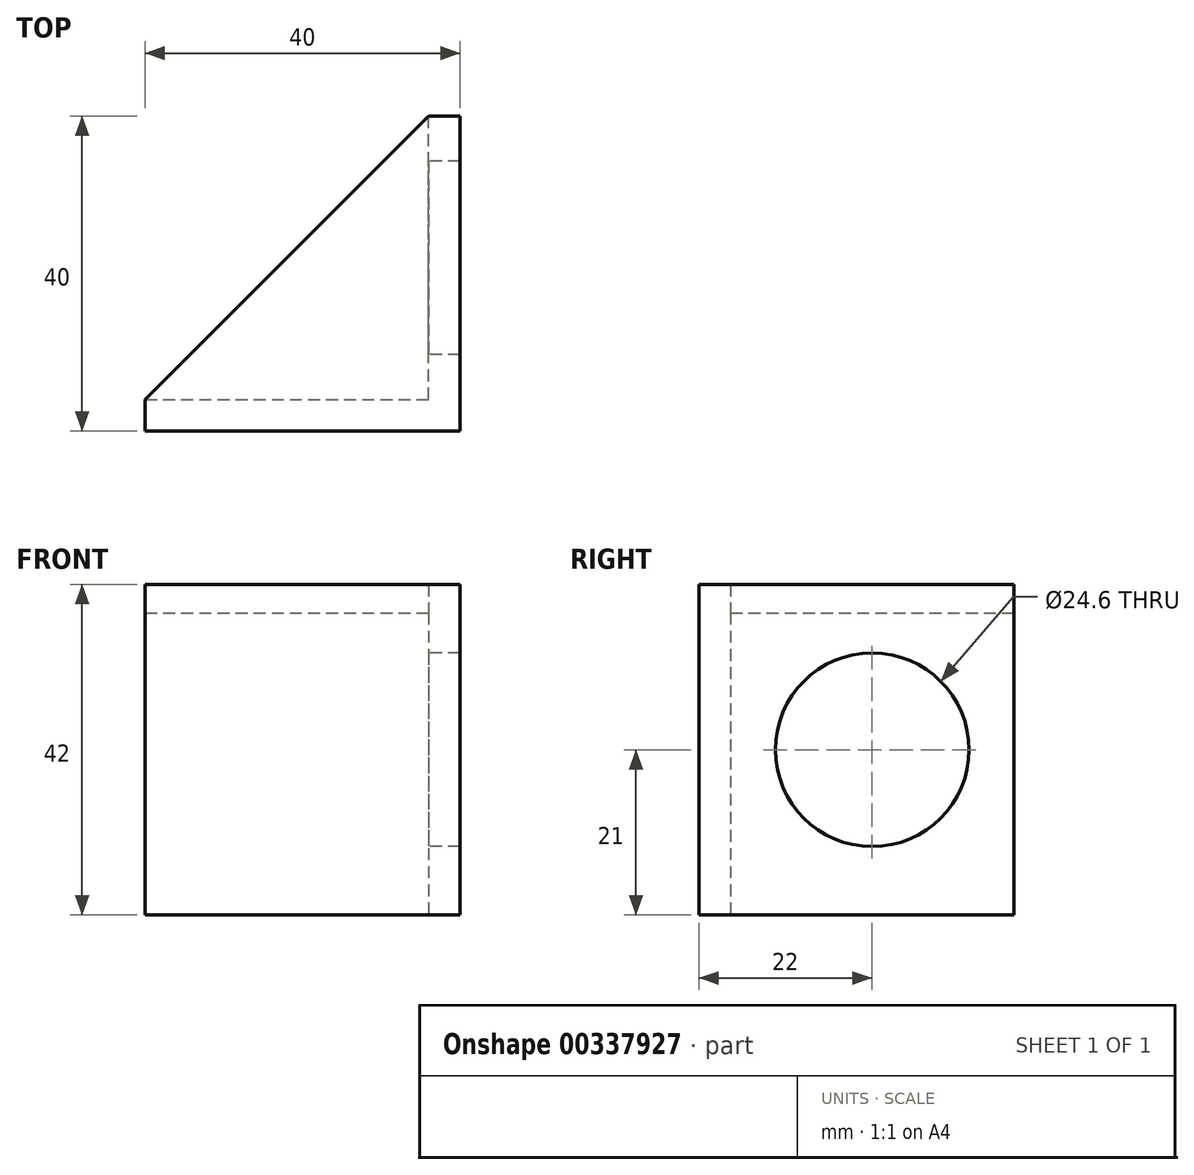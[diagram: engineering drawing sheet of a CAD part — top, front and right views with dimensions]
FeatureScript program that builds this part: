
annotation { "Feature Type Name" : "Feature", "Feature Type Description" : "" }
export const myFeature = defineFeature(function(context is Context, id is Id, definition is map)
    precondition{}
    {
        {
            var Q0;
            Q0=qCreatedBy(makeId("Top.planeOp"),FACE);
            var sketch = newSketch(context, id + "F0", { "sketchPlane" : qUnion([Q0])});
            skLineSegment(sketch, "E0", {"start": v(-40, 0) * mm, "end": v(0, 0) * mm});
            skLineSegment(sketch, "E1", {"start": v(0, 0) * mm, "end": v(0, 40) * mm});
            skLineSegment(sketch, "E2", {"start": v(-40, 0) * mm, "end": v(-40, 4) * mm});
            skLineSegment(sketch, "E3", {"start": v(-40, 4) * mm, "end": v(-4, 4) * mm});
            skLineSegment(sketch, "E4", {"start": v(-4, 4) * mm, "end": v(-4, 40) * mm});
            skLineSegment(sketch, "E5", {"start": v(-4, 40) * mm, "end": v(0, 40) * mm});
            skSolve(sketch);
        }
        {
            var Q0;
            Q0 = qSketchRegion(id + "F0", true);
            extrude(context, id + "F1", {"entities" : qUnion([Q0]), "endBound" : BoundingType.SYMMETRIC, "depth" : 42 * mm});
        }
        {
            var Q0;
            Q0=makeQuery(id+"F1.opExtrude","SWEPT_FACE",FACE,{"disambiguationData":[OSD([sQuery(id+"F0.wireOp",EDGE,"E4")])]});
            var sketch = newSketch(context, id + "F2", { "sketchPlane" : qUnion([Q0])});
            skCircle(sketch, "E6", {"center": v(-22, 0) * mm, "radius": 12.3 * mm});
            skSolve(sketch);
        }
        {
            var Q0;
            Q0=makeQuery(id+"F2.imprint","IMPRINT",FACE,{"disambiguationData":[TD([[makeQuery(id+"F2.imprint","IMPRINT",EDGE,{"derivedFrom":sQuery(id+"F2.wireOp",EDGE,"E6")}),1.0]])]});
            extrude(context, id + "F3", {"entities" : qUnion([Q0]), "operationType" : NewBodyOperationType.REMOVE, "endBound" : BoundingType.UP_TO_NEXT, "oppositeDirection" : true, "depth" : 25 * mm});
        }
        {
            var Q0;
            Q0=makeQuery(id+"F1.opExtrude","CAP_FACE",FACE,{"disambiguationData":[OSD([sQuery(id+"F0.wireOp",EDGE,"E0"),sQuery(id+"F0.wireOp",EDGE,"E1"),sQuery(id+"F0.wireOp",EDGE,"E2"),sQuery(id+"F0.wireOp",EDGE,"E3"),sQuery(id+"F0.wireOp",EDGE,"E4"),sQuery(id+"F0.wireOp",EDGE,"E5")])],"isStart":false});
            var sketch = newSketch(context, id + "F4", { "sketchPlane" : qUnion([Q0])});
            skLineSegment(sketch, "E7", {"start": v(-40, 4) * mm, "end": v(-4, 40) * mm});
            skSolve(sketch);
        }
        {
            var Q0;
            Q0=makeQuery(id+"F4.imprint","IMPRINT",FACE,{"disambiguationData":[TD([[makeQuery(id+"F4.imprint","IMPRINT",EDGE,{"derivedFrom":sQuery(id+"F4.wireOp",EDGE,"E7")}),-1.0]])]});
            extrude(context, id + "F5", {"entities" : qUnion([Q0]), "operationType" : NewBodyOperationType.ADD, "oppositeDirection" : true, "depth" : 3.6 * mm});
        }
    });
